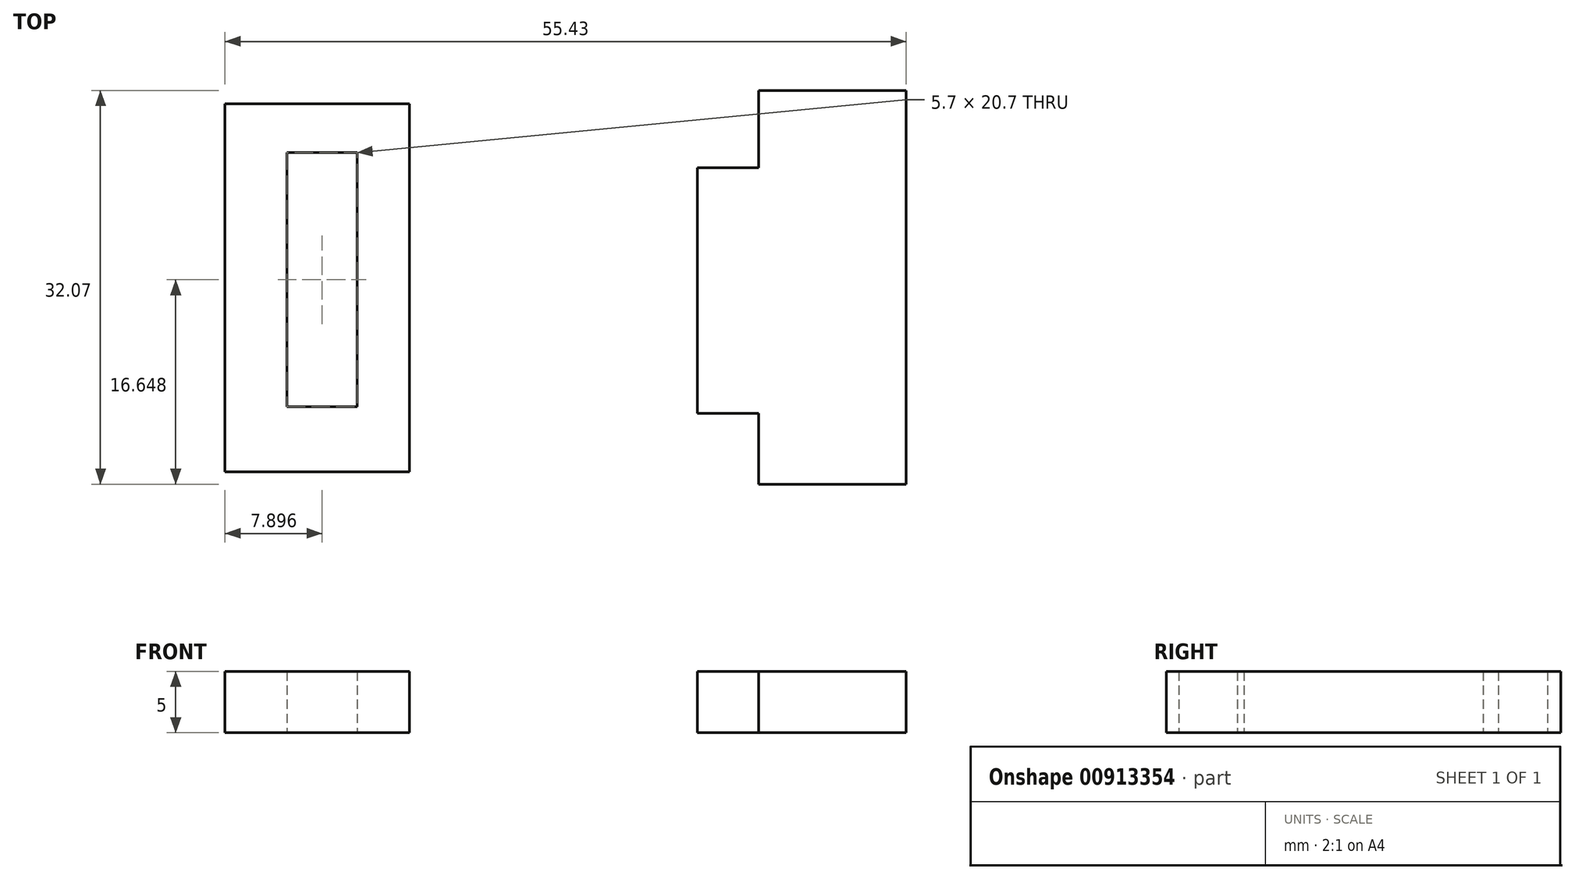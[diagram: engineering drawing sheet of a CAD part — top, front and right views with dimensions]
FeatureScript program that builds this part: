
annotation { "Feature Type Name" : "Feature", "Feature Type Description" : "" }
export const myFeature = defineFeature(function(context is Context, id is Id, definition is map)
    precondition{}
    {
        {
            var Q0;
            Q0=qCreatedBy(makeId("Top.planeOp"),FACE);
            var sketch = newSketch(context, id + "F0", { "sketchPlane" : qUnion([Q0])});
            skLineSegment(sketch, "E0.bottom", {"start": v(-25, 25.21) * mm, "end": v(-10, 25.21) * mm});
            skLineSegment(sketch, "E0.top", {"start": v(-25, -4.79) * mm, "end": v(-10, -4.79) * mm});
            skLineSegment(sketch, "E0.left", {"start": v(-25, 25.21) * mm, "end": v(-25, -4.79) * mm});
            skLineSegment(sketch, "E0.right", {"start": v(-10, 25.21) * mm, "end": v(-10, -4.79) * mm});
            skLineSegment(sketch, "E1.bottom", {"start": v(-19.95, 21.22) * mm, "end": v(-14.25, 21.22) * mm});
            skLineSegment(sketch, "E1.top", {"start": v(-19.95, 0.52) * mm, "end": v(-14.25, 0.52) * mm});
            skLineSegment(sketch, "E1.left", {"start": v(-19.95, 21.22) * mm, "end": v(-19.95, 0.52) * mm});
            skLineSegment(sketch, "E1.right", {"start": v(-14.25, 21.22) * mm, "end": v(-14.25, 0.52) * mm});
            skLineSegment(sketch, "E2", {"start": v(18.43, 0) * mm, "end": v(13.43, 0) * mm});
            skLineSegment(sketch, "E3", {"start": v(13.43, 0) * mm, "end": v(13.43, 20) * mm});
            skLineSegment(sketch, "E4", {"start": v(13.43, 20) * mm, "end": v(18.43, 20) * mm});
            skLineSegment(sketch, "E5", {"start": v(18.43, 20) * mm, "end": v(18.43, 26.3) * mm});
            skLineSegment(sketch, "E6", {"start": v(18.43, 26.3) * mm, "end": v(30.43, 26.3) * mm});
            skLineSegment(sketch, "E7", {"start": v(30.43, 26.3) * mm, "end": v(30.43, -5.78) * mm});
            skLineSegment(sketch, "E8", {"start": v(30.43, -5.78) * mm, "end": v(18.43, -5.78) * mm});
            skLineSegment(sketch, "E9", {"start": v(18.43, -5.78) * mm, "end": v(18.43, 0) * mm});
            skSolve(sketch);
        }
        {
            var Q0;
            Q0 = qSketchRegion(id + "F0", true);
            extrude(context, id + "F1", {"entities" : qUnion([Q0]), "depth" : 5 * mm, "offsetDistance" : 25 * mm});
        }
    });
